# Revit family: S-tank_Solar_SS
name_source: partatom
category: Оборудование
units: mm (PartAtom-declared; Revit-internal decimal feet)

## family parameters
Всегда вертикально = Да
Классификация = Нет
На основе рабочей плоскости = Нет
Общий = Нет
При загрузке вырезать с полостями = Нет
Размер круглого соединителя = Использовать диаметр
Тип детали = Нормальный
Точка расчета площади = Нет

## types (10) — shared parameters
ADSK_URL документации изделия = http://s-tank.ru
ADSK_Группирование = Оборудование
ADSK_Единица измерения = шт.
ADSK_Завод-изготовитель = ООО “С-ТЭНК ВОТЕР ХИТЕРС”
ADSK_Наименование = Бойлер косвенного нагрева
DN1 = 25 мм
DN2 = 15 мм
I = 1223 мм
shrf = 18 мм
Разработка семейств = https://rubim.tech

## per-type parameters (varying)
| type | A | ADSK_Код изделия | ADSK_Масса | ADSK_Обозначение | B | C | D | E | H | M | a | Диаметрcизоляцией |
| SS Solar 150 | 210 мм | 2.0001 | 51 | SSSolar 150 | 320 мм | 450 мм | 560 мм | 635 мм | 945 мм | 755 мм | 105 мм | 630 мм |
| SS Solar 200 | 220 мм | 2.0002 | 58 | SSSolar 200 | 340 мм | 520 мм | 640 мм | 715 мм | 1220 мм | 1030 мм | 105 мм | 630 мм |
| SS Solar 300 | 225 мм | 2.0003 | 70 | SSSolar 300 | 355 мм | 655 мм | 785 мм | 865 мм | 1600 мм | 1345 мм | 105 мм | 630 мм |
| SS Solar 500 | 220 мм | 2.0004 | 93 | SSSolar 500 | 350 мм | 610 мм | 740 мм | 820 мм | 1605 мм | 1340 мм | 130 мм | 780 мм |
| SS Solar 750 | 210 мм | 2.0005 | 114 | SSSolar 750 | 340 мм | 530 мм | 660 мм | 740 мм | 1630 мм | 1330 мм | 153 мм | 920 мм |
| SS Solar 1000 | 200 мм | 2.0006 | 145 | SSSolar 1000 | 390 мм | 610 мм | 800 мм | 920 мм | 2205 мм | 1915 мм | 153 мм | 920 мм |
| SS Solar 1200 | 300 мм | 2.0007 | 185 | SSSolar 1200 | 460 мм | 670 мм | 830 мм | 925 мм | 2020 мм | 1630 мм | 180 мм | 1080 мм |
| SS Solar 1500 | 300 мм | 2.0008 | 214 | SSSolar 1500 | 490 мм | 780 мм | 970 мм | 1090 мм | 2370 мм | 1980 мм | 180 мм | 1080 мм |
| SS Solar 2000 | 385 мм | 2.0009 | 260 | SSSolar 2000 | 545 мм | 905 мм | 1065 мм | 1160 мм | 2100 мм | 1715 мм | 225 мм | 1350 мм |
| SS Solar 3000 | 418 мм | 2.0010 | 0 | SSSolar 3000 | 608 мм | 918 мм | 1108 мм | 1203 мм | 2210 мм | 1748 мм | 290 мм | 1740 мм |

note: column(s) folded — value = type name in every type: ADSK_Марка
